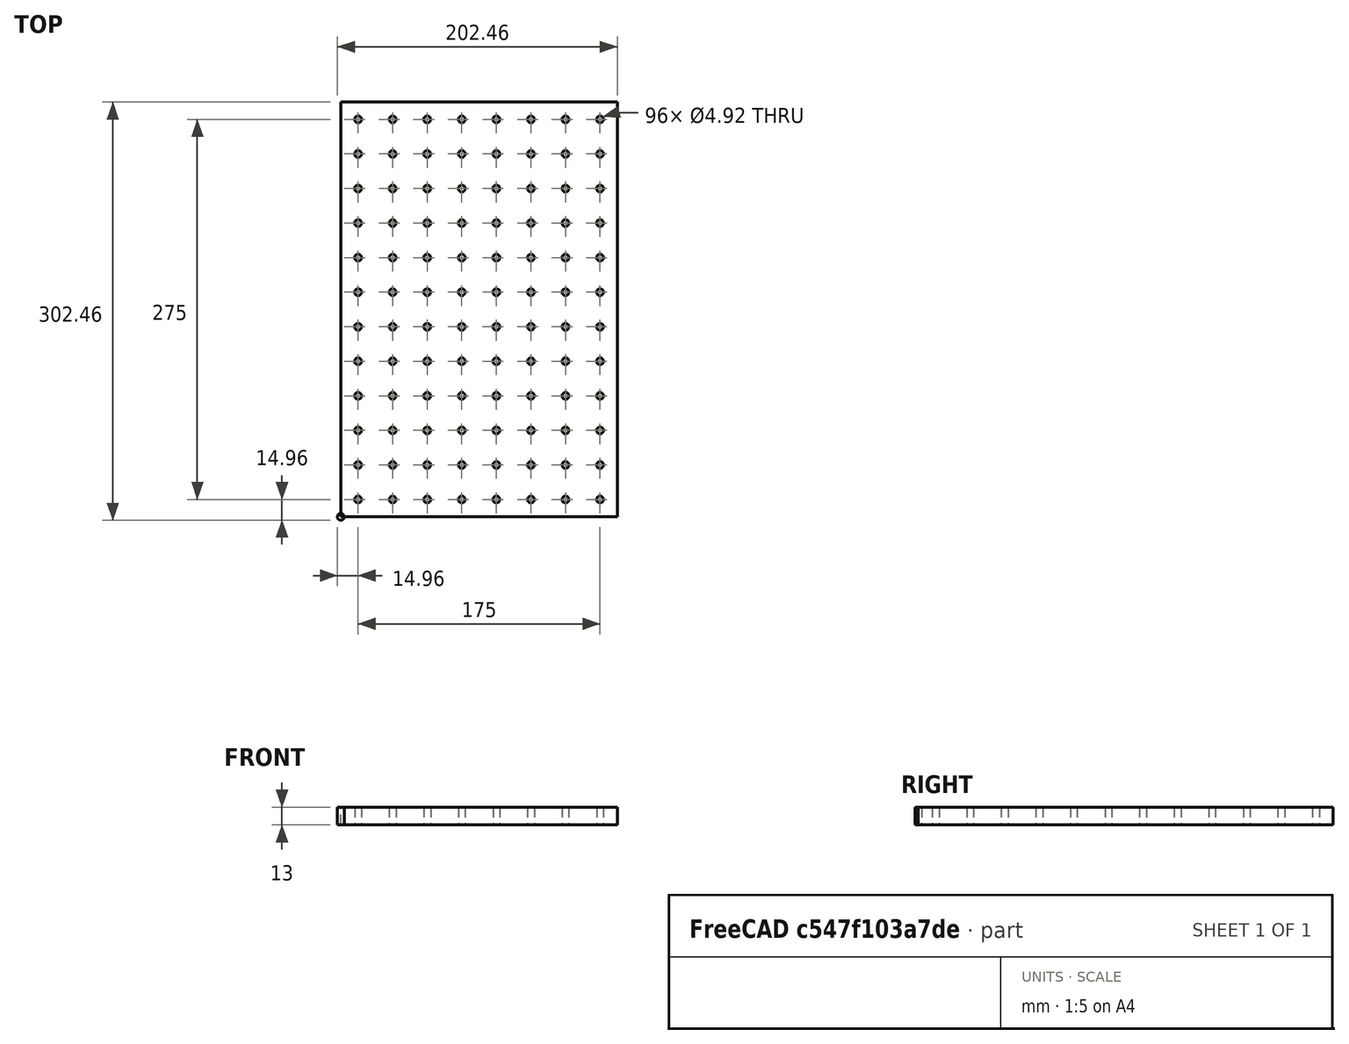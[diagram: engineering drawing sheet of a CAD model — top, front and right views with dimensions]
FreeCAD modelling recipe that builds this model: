
FCSTD DOCUMENT  (FreeCAD 0.21R33668 +7 (Git))
Label: Breadboard
License: All rights reserved
LicenseURL: https://en.wikipedia.org/wiki/All_rights_reserved
objects: Part::FeaturePython×2, Spreadsheet::Sheet×1, Part::Box×1, Part::Cut×1
note: 3 computed .brp shape members not serialized (recipe doc carries the construction recipe); baked Part::Feature solids carry a one-line shape summary decoded from their .brp

FEATURE [Spreadsheet::Sheet] Spreadsheet  label="OpticalBreadboardParameters"
  cells = A1='Optical breadboard parameters; E1='Calculated sizes; A2='Thickness; B2(thickness)=13; E2='Number of holes in A direction; F2(nHolesA)==da / ha; A3='A; B3(da)=200; E3='Number of holes in B direction; F3(nHolesB)==db / hb; A4='B; B4(db)=300; E4='Spacing from border A; F4(borderA)==(da - (nHolesA - 1) * ha) / 2; A5='Hole distance A; B5(ha)=25; E5='Spacing from border B; F5(borderB)==(db - (nHolesB - 1) * hb) / 2; A6='Hole distance B; B6(hb)=25; A8='Aperture (metric); B8(hm)=6; E8='Aperture; F8='M2; G8='M4; H8='M6; A9='Aperture pitch; B9(hpitch)=1; C9='This has to match the metric aperture; E9='Pitch; F9=0.4; G9=0.7; H9=1
FEATURE [Part::Box] Box  label="Blank"
  AttacherType = Attacher::AttachEngine3D
  Height = 13
  Length = 200
  Width = 300
  expr: Height = <<OpticalBreadboardParameters>>.thickness
  expr: Length = <<OpticalBreadboardParameters>>.da
  expr: Width = <<OpticalBreadboardParameters>>.db
FEATURE [Part::FeaturePython] ScrewTap  label="M6x13-ScrewTap"  # Fasteners workbench fastener (typed FeaturePython)
  Placement = pos=(0,0,13) rot=(0,0,1;0rad)
  diameter = 8
  diameterCustom = 6
  invert = false
  leftHanded = false
  length = 13
  matchOuter = false
  offset = 0
  pitchCustom = 1
  thread = false
  type = 2
  expr: .Placement.Base.z = <<OpticalBreadboardParameters>>.thickness
  expr: diameterCustom = <<OpticalBreadboardParameters>>.hm
  expr: length = <<OpticalBreadboardParameters>>.thickness
  expr: pitchCustom = <<OpticalBreadboardParameters>>.hpitch
FEATURE [Part::FeaturePython] Array  # Draft array (typed FeaturePython)
  AlwaysSyncPlacement = false
  Angle = 360
  ArrayType = 0
  Axis = (0,0,1)
  Base = -> ScrewTap
  Center = (0,0,0)
  Count = 96
  ExpandArray = false
  Fuse = false
  IntervalAxis = (0,0,0)
  IntervalX = (25,0,0)
  IntervalY = (0,25,0)
  IntervalZ = (0,0,100)
  NumberCircles = 3
  NumberPolar = 5
  NumberX = 8
  NumberY = 12
  NumberZ = 1
  Placement = pos=(12.5,12.5,0) rot=(0,0,1;0rad)
  PlacementList = 96 placements: [(0,0,13),(0,25,13),(0,50,13),(0,75,13),(0,100,13),(0,125,13),(0,150,13),(0,175,13),(0,200,13),(0,225,13),(0,250,13),(0,275,13),(25,0,13),(25,25,13),(25,50,13),(25,75,13),(25,100,13),(25,125,13),(25,150,13),(25,175,13),(25,200,13),(25,225,13),(25,250,13),(25,275,13),(50,0,13),(50,25,13),(50,50,13),(50,75,13),(50,100,13),(50,125,13),(50,150,13),(50,175,13),(50,200,13),(50,225,13),(50,250,13),+61 more]
  RadialDistance = 50
  ScaleList = (96) [(1,1,1),(1,1,1),(1,1,1),(1,1,1),(1,1,1),(1,1,1),(1,1,1),(1,1,1),(1,1,1),(1,1,1),(1,1,1),(1,1,1),(1,1,1),(1,1,1),(1,1,1),(1,1,1),(1,1,1),(1,1,1),+78 more]
  Symmetry = 1
  TangentialDistance = 25
  expr: .IntervalX.x = <<OpticalBreadboardParameters>>.ha
  expr: .IntervalY.y = <<OpticalBreadboardParameters>>.hb
  expr: .Placement.Base.x = <<OpticalBreadboardParameters>>.borderA
  expr: .Placement.Base.y = <<OpticalBreadboardParameters>>.borderB
  expr: NumberX = <<OpticalBreadboardParameters>>.nHolesA
  expr: NumberY = <<OpticalBreadboardParameters>>.nHolesB
FEATURE [Part::Cut] Cut  label="Breadboard"
  Base = -> Box
  Tool = -> Array
